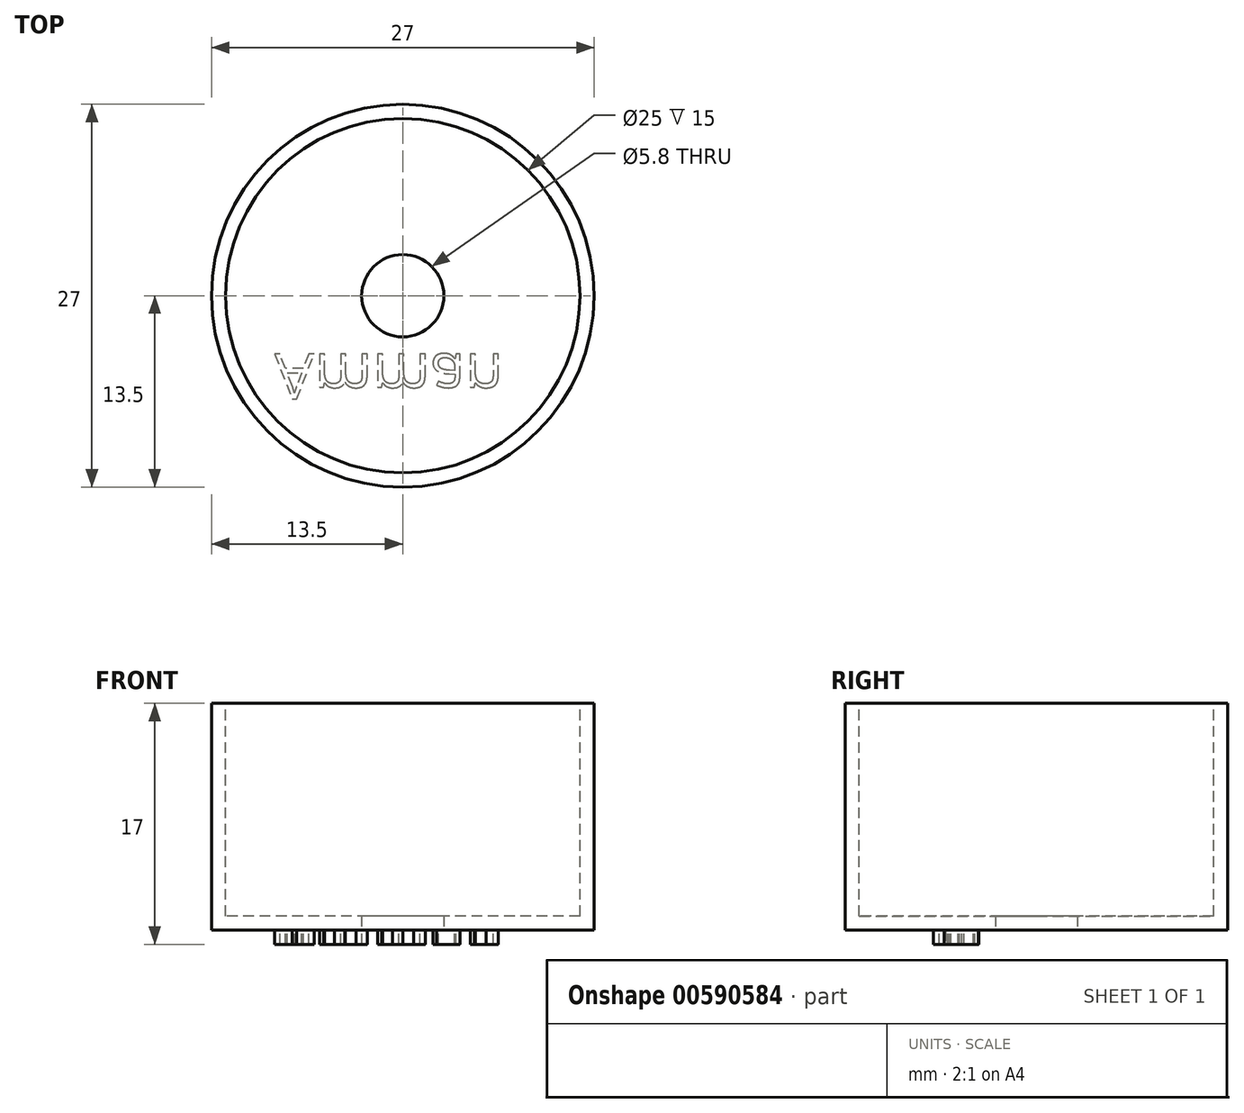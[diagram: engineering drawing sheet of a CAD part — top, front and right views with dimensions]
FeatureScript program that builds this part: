
annotation { "Feature Type Name" : "Feature", "Feature Type Description" : "" }
export const myFeature = defineFeature(function(context is Context, id is Id, definition is map)
    precondition{}
    {
        {
            var Q0;
            Q0=qCreatedBy(makeId("Top.planeOp"),FACE);
            var sketch = newSketch(context, id + "F0", { "sketchPlane" : qUnion([Q0])});
            skCircle(sketch, "E0", {"center": v(0, 0) * mm, "radius": 12.5 * mm});
            skSolve(sketch);
        }
        {
            var Q0;
            Q0=qCreatedBy(makeId("Top.planeOp"),FACE);
            var sketch = newSketch(context, id + "F1", { "sketchPlane" : qUnion([Q0])});
            skCircle(sketch, "E1", {"center": v(0, 0) * mm, "radius": 13.5 * mm});
            skSolve(sketch);
        }
        {
            var Q0;
            Q0 = qSketchRegion(id + "F1", true);
            extrude(context, id + "F2", {"entities" : qUnion([Q0]), "oppositeDirection" : true, "depth" : 16 * mm, "offsetDistance" : 25.4 * mm});
        }
        {
            var Q0;
            Q0 = qSketchRegion(id + "F0", true);
            extrude(context, id + "F3", {"entities" : qUnion([Q0]), "operationType" : NewBodyOperationType.REMOVE, "oppositeDirection" : true, "depth" : 15 * mm, "offsetDistance" : 25.4 * mm});
        }
        {
            var Q0;
            Q0=qCreatedBy(makeId("Top.planeOp"),FACE);
            cPlane(context, id + "F4", {"entities" : qUnion([Q0]), "cplaneType" : CPlaneType.OFFSET, "offset" : 16 * mm, "oppositeDirection" : true, "width" : 152.4 * mm, "height" : 152.4 * mm});
        }
        {
            var Q0;
            Q0=qCreatedBy(id+"F4.planeOp",FACE);
            var sketch = newSketch(context, id + "F5", { "sketchPlane" : qUnion([Q0])});
            skCircle(sketch, "E2", {"center": v(0, 0) * mm, "radius": 2.9 * mm});
            skSolve(sketch);
        }
        {
            var Q0;
            Q0 = qSketchRegion(id + "F5", true);
            extrude(context, id + "F6", {"entities" : qUnion([Q0]), "operationType" : NewBodyOperationType.REMOVE, "depth" : 25.4 * mm, "offsetDistance" : 25.4 * mm});
        }
        {
            var Q0;
            Q0=makeQuery(id+"F2.opExtrude","CAP_FACE",FACE,{"disambiguationData":[OSD([sQuery(id+"F1.wireOp",EDGE,"E1")])],"isStart":false});
            var sketch = newSketch(context, id + "F7", { "sketchPlane" : qUnion([Q0])});
            skText(sketch, "E3", { "text": "Amman", "fontName": "OpenSans-Regular.ttf"});
            const initialGuessF7  = {"E3": [-0.00904, 0.00411, 1, 0, 0.00317]};
            skSetInitialGuess(sketch, initialGuessF7);
            skSolve(sketch);
        }
        {
            var Q0;
            Q0 = qSketchRegion(id + "F7", true);
            extrude(context, id + "F8", {"entities" : qUnion([Q0]), "operationType" : NewBodyOperationType.ADD, "depth" : 1 * mm, "offsetDistance" : 25.4 * mm});
        }
    });
